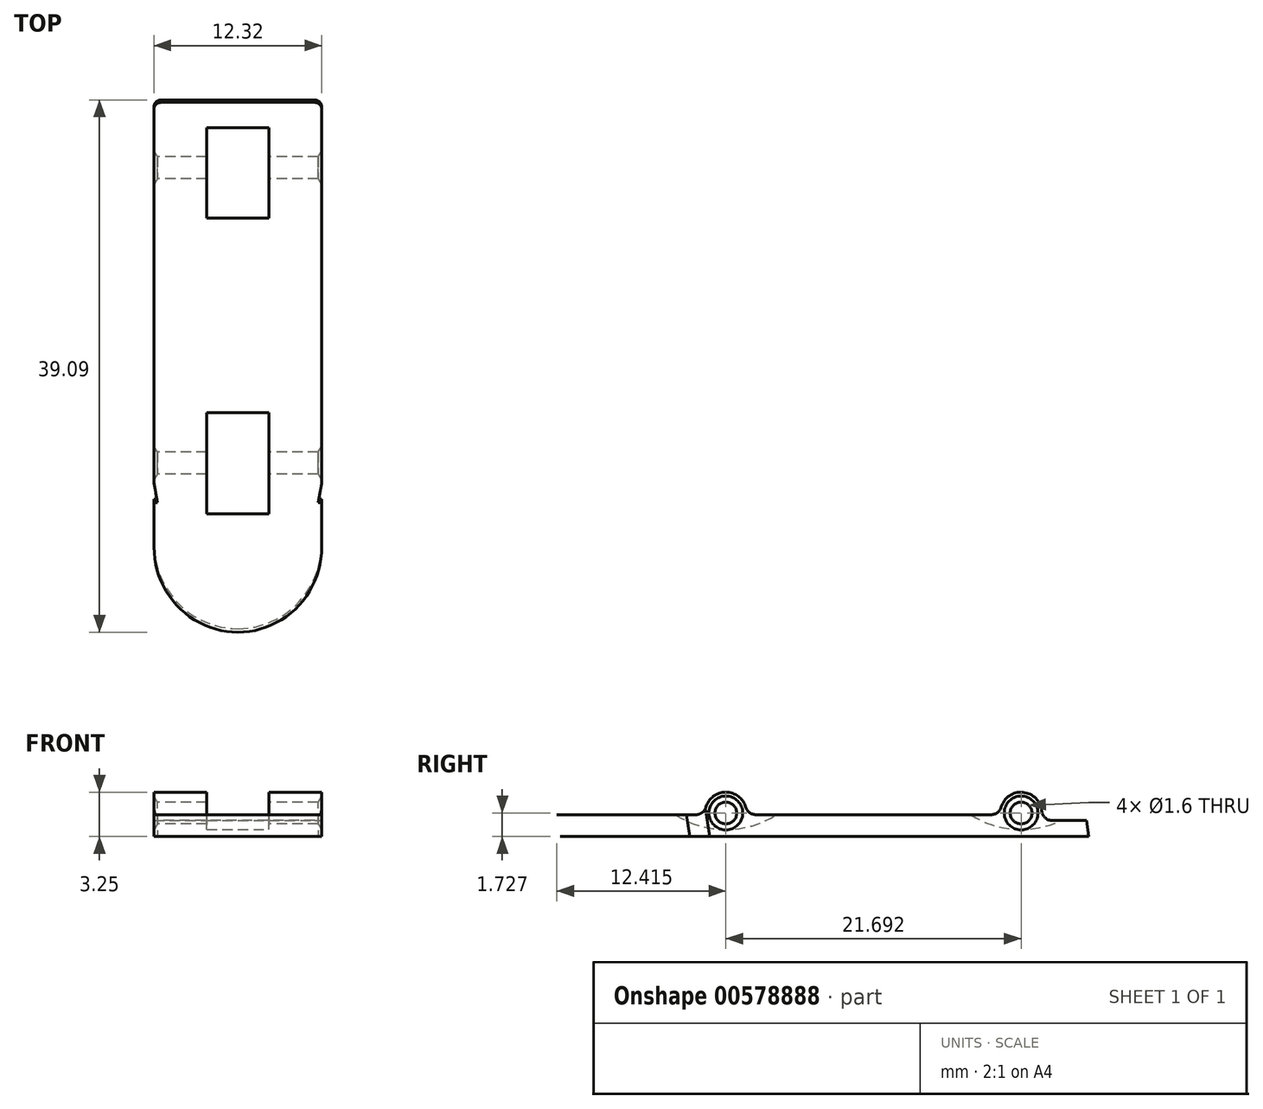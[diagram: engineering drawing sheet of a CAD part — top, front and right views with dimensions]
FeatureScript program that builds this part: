
annotation { "Feature Type Name" : "Feature", "Feature Type Description" : "" }
export const myFeature = defineFeature(function(context is Context, id is Id, definition is map)
    precondition{}
    {
        {
            var Q0;
            Q0=qCreatedBy(makeId("Right.planeOp"),FACE);
            var sketch = newSketch(context, id + "F0", { "sketchPlane" : qUnion([Q0])});
            skLineSegment(sketch, "E0", {"start": v(-19.42, 0) * mm, "end": v(19.42, 0) * mm});
            skPoint(sketch, "E1", {"position": v(0, 0) * mm});
            skLineSegment(sketch, "E2", {"start": v(-19.42, 0) * mm, "end": v(-19.67, 1.6) * mm});
            skLineSegment(sketch, "E3", {"start": v(19.42, 0) * mm, "end": v(19.23, 1.17) * mm});
            skLineSegment(sketch, "E4", {"start": v(-19.67, 1.6) * mm, "end": v(-8.77, 1.6) * mm});
            skPoint(sketch, "E4.endSnap0", {"position": v(-19.67, 1.6) * mm});
            skPoint(sketch, "E5.orphan", {"position": v(-19.92, 3.2) * mm});
            skPoint(sketch, "E6.orphan", {"position": v(21.51, 1.6) * mm});
            skArc(sketch, "E7", {"start": v(15.85, 1.17) * mm, "mid": v(14.66, 3.23) * mm, "end": v(12.92, 1.6) * mm});
            skArc(sketch, "E8", {"start": v(-5.74, 1.6) * mm, "mid": v(-7.26, 3.25) * mm, "end": v(-8.77, 1.6) * mm});
            skLineSegment(sketch, "E9", {"start": v(14.3, 2.53) * mm, "end": v(14.9, -1.15) * mm, "construction": true});
            skLineSegment(sketch, "E10.trimOffspring", {"start": v(-5.74, 1.6) * mm, "end": v(12.92, 1.6) * mm});
            skCircle(sketch, "E11", {"center": v(-7.26, 1.73) * mm, "radius": 0.8 * mm});
            skCircle(sketch, "E12", {"center": v(14.44, 1.73) * mm, "radius": 0.8 * mm});
            skLineSegment(sketch, "E13", {"start": v(19.23, 1.17) * mm, "end": v(15.85, 1.17) * mm});
            skSolve(sketch);
        }
        {
            var Q0;
            Q0=makeQuery(id+"F0.imprint","IMPRINT",FACE,{"disambiguationData":[TD([[makeQuery(id+"F0.imprint","IMPRINT",EDGE,{"derivedFrom":sQuery(id+"F0.wireOp",EDGE,"E0")}),1.0]])]});
            extrude(context, id + "F1", {"entities" : qUnion([Q0]), "endBound" : BoundingType.SYMMETRIC, "depth" : 12.32 * mm});
        }
        {
            var Q0;
            Q0=makeQuery(id+"F1.opExtrude","SWEPT_EDGE",EDGE,{"disambiguationData":[OSD([sQuery(id+"F0.wireOp",EDGE,"E4"),sQuery(id+"F0.wireOp",EDGE,"E8")])]});
            var Q1;
            Q1=makeQuery(id+"F1.opExtrude","SWEPT_EDGE",EDGE,{"disambiguationData":[OSD([sQuery(id+"F0.wireOp",EDGE,"E8"),sQuery(id+"F0.wireOp",EDGE,"E10.trimOffspring")])]});
            var Q2;
            Q2=makeQuery(id+"F1.opExtrude","SWEPT_EDGE",EDGE,{"disambiguationData":[OSD([sQuery(id+"F0.wireOp",EDGE,"E7"),sQuery(id+"F0.wireOp",EDGE,"E10.trimOffspring")])]});
            var Q3;
            Q3=makeQuery(id+"F1.opExtrude","SWEPT_EDGE",EDGE,{"disambiguationData":[OSD([sQuery(id+"F0.wireOp",EDGE,"E7"),sQuery(id+"F0.wireOp",EDGE,"E13")])]});
            fillet(context, id + "F2", {"entities" : qUnion([Q0, Q1, Q2, Q3]), "radius" : 0.76 * mm, "tangentPropagation" : true, "allowEdgeOverflow" : false});
        }
        {
            var Q0;
            Q0=makeQuery(id+"F1.opExtrude","CAP_EDGE",EDGE,{"disambiguationData":[OSD([sQuery(id+"F0.wireOp",EDGE,"E11")])],"isStart":false});
            var Q1;
            Q1=makeQuery(id+"F1.opExtrude","CAP_EDGE",EDGE,{"disambiguationData":[OSD([sQuery(id+"F0.wireOp",EDGE,"E12")])],"isStart":false});
            var Q2;
            Q2=makeQuery(id+"F1.opExtrude","CAP_EDGE",EDGE,{"disambiguationData":[OSD([sQuery(id+"F0.wireOp",EDGE,"E11")])],"isStart":true});
            chamfer(context, id + "F3", {"entities" : qUnion([Q0, Q1, Q2]), "chamferType" : ChamferType.OFFSET_ANGLE, "width" : 0.25 * mm, "oppositeDirection" : false, "angle" : 60 * degree, "tangentPropagation" : true});
        }
        {
            var Q0;
            Q0=makeQuery(id+"F1.opExtrude","CAP_EDGE",EDGE,{"disambiguationData":[OSD([sQuery(id+"F0.wireOp",EDGE,"E12")])],"isStart":true});
            chamfer(context, id + "F4", {"entities" : qUnion([Q0]), "chamferType" : ChamferType.OFFSET_ANGLE, "width" : 0.25 * mm, "oppositeDirection" : true, "angle" : 60 * degree});
        }
        {
            var Q0;
            Q0=qCreatedBy(makeId("Right.planeOp"),FACE);
            var sketch = newSketch(context, id + "F5", { "sketchPlane" : qUnion([Q0])});
            skPoint(sketch, "E14.0", {"position": v(-7.26, 1.73) * mm});
            skPoint(sketch, "E15.0", {"position": v(14.44, 1.73) * mm});
            skLineSegment(sketch, "E16", {"start": v(-7.26, -1.76) * mm, "end": v(-7.26, 12.67) * mm, "construction": true});
            skLineSegment(sketch, "E17", {"start": v(14.44, -3.15) * mm, "end": v(14.44, 12.85) * mm, "construction": true});
            skArc(sketch, "E18", {"start": v(-13.5, 4.52) * mm, "mid": v(-7.7, 0.52) * mm, "end": v(-1.43, 3.75) * mm});
            skArc(sketch, "E19", {"start": v(8.6, 3.76) * mm, "mid": v(14.4, 0.5) * mm, "end": v(20.23, 3.7) * mm});
            skPoint(sketch, "E20", {"position": v(-7.26, 0.5) * mm});
            skLineSegment(sketch, "E21", {"start": v(-13.5, 4.52) * mm, "end": v(-1.43, 3.75) * mm});
            skLineSegment(sketch, "E22", {"start": v(8.6, 3.76) * mm, "end": v(20.23, 3.7) * mm});
            skSolve(sketch);
        }
        {
            var Q0;
            Q0=qSketchRegion(id+"F5",true);
            extrude(context, id + "F6", {"entities" : qUnion([Q0]), "operationType" : NewBodyOperationType.REMOVE, "endBound" : BoundingType.SYMMETRIC, "oppositeDirection" : true, "depth" : 4.57 * mm});
        }
        {
            var Q0;
            Q0=sQuery(id+"F0.wireOp",EDGE,"E2");
            var Q1;
            Q1=sQuery(id+"F0.wireOp",VERTEX,"E8.center");
            cPlane(context, id + "F7", {"entities" : qUnion([Q0, Q1]), "cplaneType" : CPlaneType.LINE_POINT, "offset" : 152.4 * mm, "width" : 152.4 * mm, "height" : 152.4 * mm});
        }
        {
            var Q0;
            Q0=makeQuery(id+"F1.opExtrude","CAP_EDGE",EDGE,{"disambiguationData":[OSD([sQuery(id+"F0.wireOp",EDGE,"E3")])],"isStart":false});
            var Q1;
            Q1=makeQuery(id+"F1.opExtrude","CAP_EDGE",EDGE,{"disambiguationData":[OSD([sQuery(id+"F0.wireOp",EDGE,"E3")])],"isStart":true});
            fillet(context, id + "F8", {"entities" : qUnion([Q0, Q1]), "radius" : 0.5 * mm, "tangentPropagation" : true, "allowEdgeOverflow" : false});
        }
        {
            var Q0;
            Q0=makeQuery(id+"F1.opExtrude","CAP_EDGE",EDGE,{"disambiguationData":[OSD([sQuery(id+"F0.wireOp",EDGE,"E2")])],"isStart":false});
            var Q1;
            Q1=makeQuery(id+"F1.opExtrude","CAP_EDGE",EDGE,{"disambiguationData":[OSD([sQuery(id+"F0.wireOp",EDGE,"E2")])],"isStart":true});
            fillet(context, id + "F9", {"entities" : qUnion([Q0, Q1]), "radius" : 6.17 * mm, "tangentPropagation" : true, "allowEdgeOverflow" : false});
        }
        {
            var Q0;
            Q0=qCreatedBy(id+"F7.planeOp",FACE);
            var sketch = newSketch(context, id + "F10", { "sketchPlane" : qUnion([Q0])});
            skLineSegment(sketch, "E23", {"start": v(6.16, -9.78) * mm, "end": v(5.9, -9.78) * mm});
            skLineSegment(sketch, "E24", {"start": v(5.9, -9.78) * mm, "end": v(6.16, -8.34) * mm});
            skLineSegment(sketch, "E25", {"start": v(-6.16, -9.78) * mm, "end": v(-5.9, -9.78) * mm});
            skLineSegment(sketch, "E26", {"start": v(-5.9, -9.78) * mm, "end": v(-6.16, -8.34) * mm});
            skPoint(sketch, "E27.orphan", {"position": v(-6.16, -9.08) * mm});
            skPoint(sketch, "E28.orphan", {"position": v(6.16, -9.08) * mm});
            skPoint(sketch, "E29.0", {"position": v(0, -19.18) * mm});
            skLineSegment(sketch, "E30.0", {"start": v(-6.16, -13) * mm, "end": v(-6.16, -8.34) * mm});
            skLineSegment(sketch, "E31.0", {"start": v(6.16, -13) * mm, "end": v(6.16, -8.34) * mm});
            skSolve(sketch);
        }
        {
            var Q0;
            Q0=qSketchRegion(id+"F10",true);
            extrude(context, id + "F11", {"entities" : qUnion([Q0]), "operationType" : NewBodyOperationType.REMOVE, "endBound" : BoundingType.SYMMETRIC, "depth" : 25.4 * mm});
        }
    });
